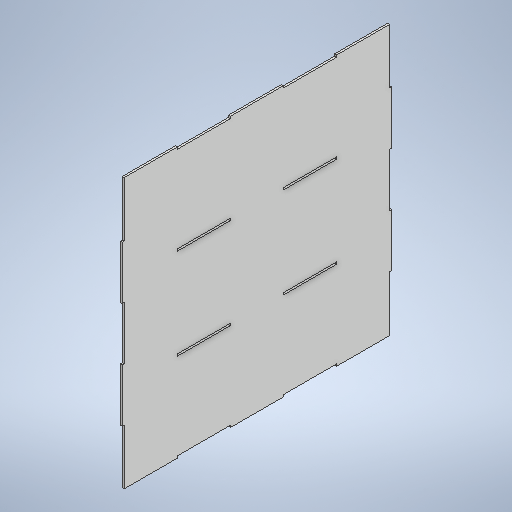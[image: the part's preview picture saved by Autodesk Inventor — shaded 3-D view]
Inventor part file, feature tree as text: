
AUTODESK INVENTOR PART (.ipt)
format: ipt  version: 2025.1 (Build 291241020, 241B)  size: 279,040 bytes
history: native  units: mm
features: extrude x1, sketch x1
ambient origin geometry x8: Origin, YZ Plane, XZ Plane, XY Plane, X Axis, Y Axis, Z Axis, Center Point
bodies: Solid1 (feature_tree)
feature tree (2):
  extrude  "Extrusion1"  Depth=400.0mm
  sketch  "Sketch1"  dims[d0=400.0mm d1=400.0mm d2=3.0mm d3=80.0mm d4=3.0mm d5=80.0mm d6=80.0mm d7=3.0mm d8=80.0mm d13=3.0mm d14=80.0mm d15=3.0mm d16=0.0mm d17=130.0mm d18=3.0mm d19=134.0mm d20=3.0mm d21=80.0mm d22=80.0mm d24=80.0mm d25=3.0mm]
